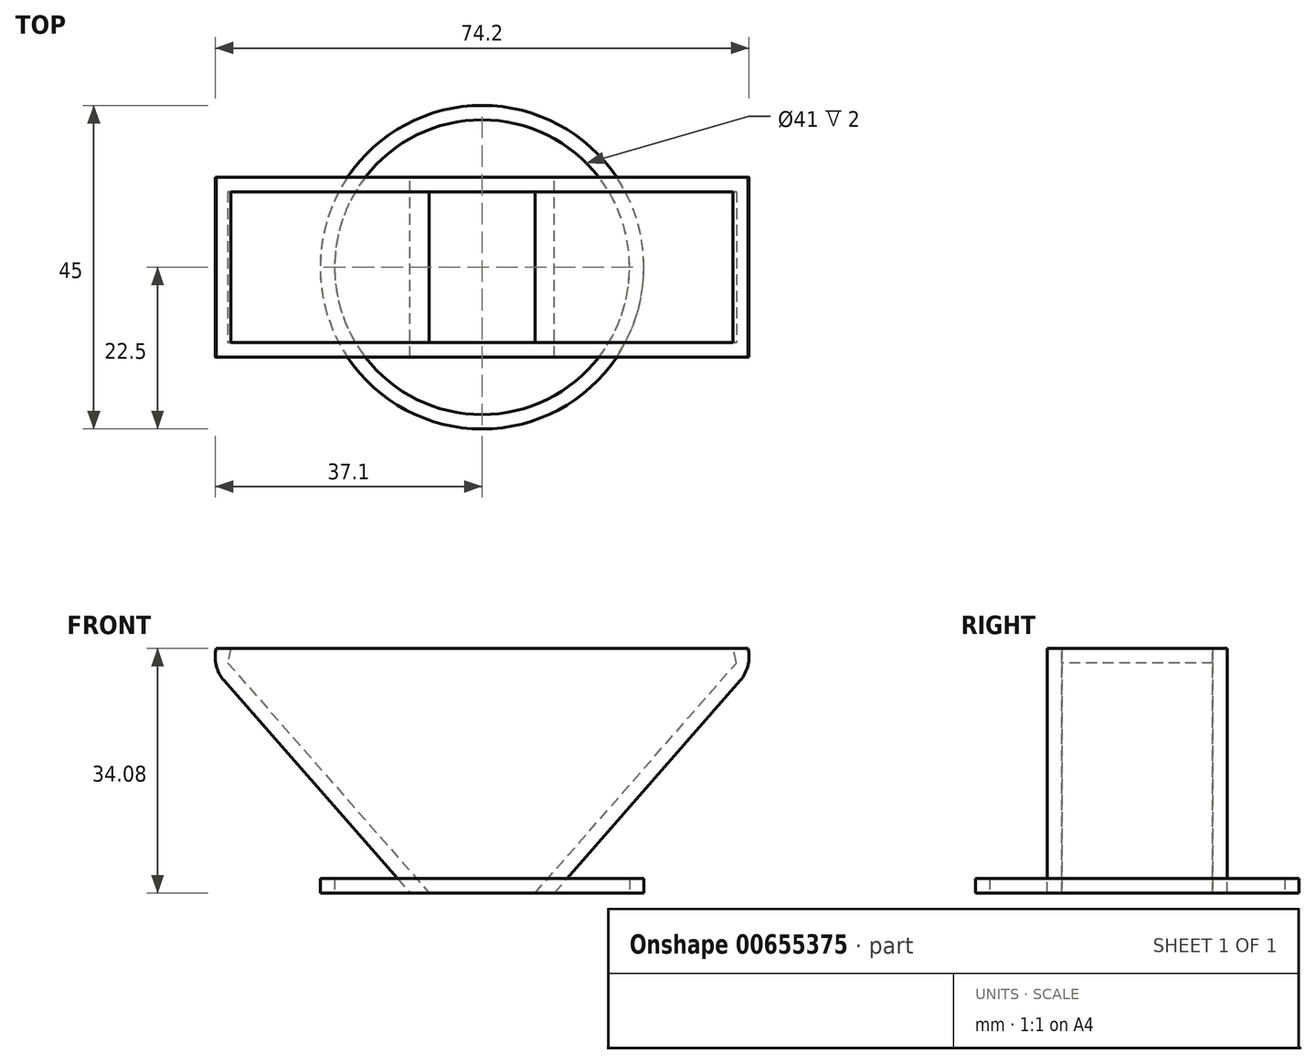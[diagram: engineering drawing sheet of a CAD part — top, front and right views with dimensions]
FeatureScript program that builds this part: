
annotation { "Feature Type Name" : "Feature", "Feature Type Description" : "" }
export const myFeature = defineFeature(function(context is Context, id is Id, definition is map)
    precondition{}
    {
        {
            var Q0;
            Q0=qCreatedBy(makeId("Top.planeOp"),FACE);
            var sketch = newSketch(context, id + "F0", { "sketchPlane" : qUnion([Q0])});
            skCircle(sketch, "E0", {"center": v(0, 0) * mm, "radius": 22.5 * mm});
            skCircle(sketch, "E1.0", {"center": v(0, 0) * mm, "radius": 20.5 * mm});
            skCircle(sketch, "E2.0", {"center": v(0, 0) * mm, "radius": 18.5 * mm});
            skSolve(sketch);
        }
        {
            var Q0;
            Q0=makeQuery(id+"F0.imprint","IMPRINT",FACE,{"disambiguationData":[TD([[makeQuery(id+"F0.imprint","IMPRINT",EDGE,{"derivedFrom":sQuery(id+"F0.wireOp",EDGE,"E0")}),1.0]])]});
            extrude(context, id + "F1", {"entities" : qUnion([Q0]), "depth" : 2 * mm, "offsetDistance" : 25 * mm});
        }
        {
            var Q0;
            Q0=qCreatedBy(makeId("Front.planeOp"),FACE);
            var sketch = newSketch(context, id + "F2", { "sketchPlane" : qUnion([Q0])});
            skLineSegment(sketch, "E3", {"start": v(0, 0) * mm, "end": v(0, 63) * mm, "construction": true});
            skArc(sketch, "E4", {"start": v(36.95, 34.03) * mm, "mid": v(0, 63) * mm, "end": v(-36.95, 34.03) * mm});
            skLineSegment(sketch, "E5", {"start": v(-35.86, 29.55) * mm, "end": v(-10, 0) * mm});
            skLineSegment(sketch, "E6", {"start": v(10.01, -0.05) * mm, "end": v(35.86, 29.55) * mm});
            skPoint(sketch, "E7.visualSharp", {"position": v(-37.5, 31.42) * mm});
            skArc(sketch, "E7.filletArc", {"start": v(-36.95, 34.03) * mm, "mid": v(-36.96, 31.66) * mm, "end": v(-35.86, 29.55) * mm});
            skPoint(sketch, "E8.visualSharp", {"position": v(37.5, 31.42) * mm});
            skArc(sketch, "E8.filletArc", {"start": v(35.86, 29.55) * mm, "mid": v(36.96, 31.66) * mm, "end": v(36.95, 34.03) * mm});
            skLineSegment(sketch, "E9", {"start": v(0, 0) * mm, "end": v(10, 0) * mm, "construction": true});
            skLineSegment(sketch, "E10", {"start": v(-10, 0) * mm, "end": v(10.01, -0.05) * mm});
            skLineSegment(sketch, "E11", {"start": v(-36.95, 34.03) * mm, "end": v(36.95, 34.03) * mm, "construction": true});
            skLineSegment(sketch, "E12", {"start": v(36.95, 34.03) * mm, "end": v(36.96, 63) * mm});
            skLineSegment(sketch, "E13", {"start": v(36.96, 63) * mm, "end": v(36.96, 53) * mm, "construction": true});
            skLineSegment(sketch, "E14", {"start": v(-36.95, 34.03) * mm, "end": v(-36.95, 63) * mm});
            skLineSegment(sketch, "E15", {"start": v(-36.95, 63) * mm, "end": v(36.96, 63) * mm});
            skLineSegment(sketch, "E16.0", {"start": v(-35.36, 32) * mm, "end": v(-7.34, 0) * mm});
            skArc(sketch, "E16.1", {"start": v(35.36, 32) * mm, "mid": v(0, 61) * mm, "end": v(-35.36, 32) * mm});
            skLineSegment(sketch, "E16.2", {"start": v(7.36, -0.04) * mm, "end": v(35.36, 32) * mm});
            skLineSegment(sketch, "E17", {"start": v(35.36, 32) * mm, "end": v(36.95, 34.03) * mm});
            skLineSegment(sketch, "E18", {"start": v(-35.36, 32) * mm, "end": v(-36.95, 34.03) * mm});
            skLineSegment(sketch, "E19", {"start": v(-36.95, 34.03) * mm, "end": v(36.95, 34.03) * mm});
            skSolve(sketch);
        }
        {
            var Q0;
            {var subQ1=sQuery(id+"F2.wireOp",EDGE,"E5");Q0=makeQuery(id+"F2.imprint","IMPRINT",FACE,{"disambiguationData":[TD([[makeQuery(id+"F2.imprint","IMPRINT",EDGE,{"derivedFrom":subQ1}),1.0]])]});}
            var Q1;
            Q1=makeQuery(id+"F2.imprint","IMPRINT",FACE,{"disambiguationData":[TD([[makeQuery(id+"F2.imprint","IMPRINT",EDGE,{"derivedFrom":sQuery(id+"F2.wireOp",EDGE,"E16.1")}),-1.0]])]});
            var Q2;
            {var subQ2=sQuery(id+"F2.wireOp",EDGE,"E6");Q2=makeQuery(id+"F2.imprint","IMPRINT",FACE,{"disambiguationData":[TD([[makeQuery(id+"F2.imprint","IMPRINT",EDGE,{"derivedFrom":subQ2}),1.0]])]});}
            var Q3;
            {var subQ0=sQuery(id+"F2.wireOp",EDGE,"E16.0");Q3=makeQuery(id+"F2.imprint","IMPRINT",FACE,{"disambiguationData":[TD([[makeQuery(id+"F2.imprint","IMPRINT",EDGE,{"derivedFrom":subQ0}),1.0]])]});}
            extrude(context, id + "F3", {"entities" : qUnion([Q0, Q1, Q2, Q3]), "depth" : 25 * mm, "offsetDistance" : 25 * mm, "symmetric" : true});
        }
        {
            var Q0;
            {var subQ0=sQuery(id+"F2.wireOp",EDGE,"E19");var subQ1=sQuery(id+"F2.wireOp",EDGE,"E16.1");var subQ2=makeQuery(id+"F2.imprint","INTERSECT",VERTEX,{"disambiguationData":[OD(0.0)],"derivedFrom":[subQ1,subQ0]});Q0=makeQuery(id+"F2.imprint","IMPRINT",FACE,{"disambiguationData":[TD([[makeQuery(id+"F2.imprint","IMPRINT",EDGE,{"disambiguationData":[TD([[subQ2,-1.0]])],"derivedFrom":subQ1}),1.0]])]});}
            var Q1;
            {var subQ0=sQuery(id+"F2.wireOp",EDGE,"E19");var subQ4=sQuery(id+"F2.wireOp",EDGE,"E16.1");var subQ6=makeQuery(id+"F2.imprint","INTERSECT",VERTEX,{"disambiguationData":[OD(0.0)],"derivedFrom":[subQ4,subQ0]});Q1=makeQuery(id+"F2.imprint","IMPRINT",FACE,{"disambiguationData":[TD([[makeQuery(id+"F2.imprint","IMPRINT",EDGE,{"disambiguationData":[TD([[subQ6,-1.0]])],"derivedFrom":subQ4}),-1.0]])]});}
            var Q2;
            {var subQ0=sQuery(id+"F2.wireOp",EDGE,"E12");Q2=makeQuery(id+"F2.imprint","IMPRINT",FACE,{"disambiguationData":[TD([[makeQuery(id+"F2.imprint","IMPRINT",EDGE,{"derivedFrom":subQ0}),1.0]])]});}
            var Q3;
            {var subQ1=sQuery(id+"F2.wireOp",EDGE,"E16.0");Q3=makeQuery(id+"F2.imprint","IMPRINT",FACE,{"disambiguationData":[TD([[makeQuery(id+"F2.imprint","IMPRINT",EDGE,{"derivedFrom":subQ1}),1.0]])]});}
            extrude(context, id + "F4", {"entities" : qUnion([Q0, Q1, Q2, Q3]), "operationType" : NewBodyOperationType.REMOVE, "oppositeDirection" : true, "depth" : 21 * mm, "offsetDistance" : 25 * mm, "symmetric" : true});
        }
    });
